# Revit family: 1698-W-3
name_source: partatom
category: Mechanical Equipment
revit_build: Autodesk Revit MEP 2016 (Build: 20150220_1215(x64)
units: mm (PartAtom-declared; Revit-internal decimal feet)

## family parameters
Cut with Voids When Loaded = No
Host = Face
OmniClass Number = 23.45.05.14.34
OmniClass Title = Security Plumbing Fixtures
Part Type = Normal
Room Calculation Point = No
Round Connector Dimension = Use Diameter
Shared = Yes

## types (1)
- 1698-W-3
    Amperage = 0
    CW Connection = Yes
    Default Elevation = 0 "
    Description = Squat Toilet
    HW Connection = No
    Manufacturer = Acorn Engineering Co
    Material = Stainless Steel
    Model = 1698-W-3
    OVERALL DEPTH = 25.75
    OVERALL SIZE HEIGHT = 0
    OVERALL SIZE WIDTH = 19.5
    Revised Date = 12/05/19
    Tempered Water Connection = No
    URL = https://www.acorneng.com
    Vent Connection = No
    Voltage = 0
    Waste Connection = Yes

## geometry (parser evidence)
native form markers: Sweep x3
no freeform markers — native parametric forms only
